# Revit family: Bernhardt_Design-Tables-Multipurpose-Intersection_stationary
name_source: partatom
category: Furniture
units: mm (PartAtom-declared; Revit-internal decimal feet)

## family parameters
Always vertical = Yes
Cut with Voids When Loaded = No
OmniClass Number = 23.40.20.00
OmniClass Title = General Furniture and Specialties
Room Calculation Point = No
Shared = No
Work Plane-Based = No

## types (90) — shared parameters
Default Elevation = 0.000"
Manufacturer = Bernhardt Design
Model = Intersection
Modesty Position = 3.720"
URL = http://www.bernhardtdesign.com

## per-type parameters (varying)
| type | Catalog | Centerleg Visibility | Modesty Length Half | Modesty Panel Visibility | Rail Length | Rail Length Half | Rail Width Half | SKU | Table Length | Table Length Half | Table Width | Table Width Half | Two Centerleg Visibility |
| Intersection - FAA - 36x36 stationary | INS-FAA | No | 13.125" | No | 35.024" | 17.512" | 17.512" | INS-FAA | 36.000" | 18.000" | 36.000" | 18.000" | No |
| Intersection - FBB - 42x42 stationary | INS-FBB | No | 16.125" | No | 41.024" | 20.512" | 20.512" | INS-FBB | 42.000" | 21.000" | 42.000" | 21.000" | No |
| Intersection - FCC - 48x48 stationary | INS-FCC | No | 19.125" | No | 47.024" | 23.512" | 23.512" | INS-FCC | 48.000" | 24.000" | 48.000" | 24.000" | No |
| Intersection - FDD - 54x54 stationary w/ modesty | INS-FDD | No | 22.125" | Yes | 53.024" | 26.512" | 26.512" | INS-FDD | 54.000" | 27.000" | 54.000" | 27.000" | No |
| Intersection - FDD - 54x54 stationary | INS-FDD | No | 22.125" | No | 53.024" | 26.512" | 26.512" | INS-FDD | 54.000" | 27.000" | 54.000" | 27.000" | No |
| Intersection - FVC - 48x24 stationary | INS-FVC | No | 19.125" | No | 47.024" | 23.512" | 11.512" | INS-FVC | 48.000" | 24.000" | 24.000" | 12.000" | No |
| Intersection - FVD - 54x24 stationary | INS-FVD | No | 22.125" | No | 53.024" | 26.512" | 11.512" | INS-FVD | 54.000" | 27.000" | 24.000" | 12.000" | No |
| Intersection - FVD - 54x24 stationary w/ modesty | INS-FVD | No | 22.125" | Yes | 53.024" | 26.512" | 11.512" | INS-FVD | 54.000" | 27.000" | 24.000" | 12.000" | No |
| Intersection - FVE - 60x24 stationary | INS-FVE | No | 25.125" | No | 59.024" | 29.512" | 11.512" | INS-FVE | 60.000" | 30.000" | 24.000" | 12.000" | No |
| Intersection - FVE - 60x24 stationary w/ modesty | INS-FVE | No | 25.125" | Yes | 59.024" | 29.512" | 11.512" | INS-FVE | 60.000" | 30.000" | 24.000" | 12.000" | No |
| Intersection - FVF - 66x24 stationary | INS-FVF | No | 28.125" | No | 65.024" | 32.512" | 11.512" | INS-FVF | 66.000" | 33.000" | 24.000" | 12.000" | No |
| Intersection - FVF - 66x24 stationary w/ modesty | INS-FVF | No | 28.125" | Yes | 65.024" | 32.512" | 11.512" | INS-FVF | 66.000" | 33.000" | 24.000" | 12.000" | No |
| Intersection - FVG - 72x24 stationary | INS-FVG | No | 31.125" | No | 71.024" | 35.512" | 11.512" | INS-FVG | 72.000" | 36.000" | 24.000" | 12.000" | No |
| Intersection - FVG - 72x24 stationary w/ modesty | INS-FVG | No | 31.125" | Yes | 71.024" | 35.512" | 11.512" | INS-FVG | 72.000" | 36.000" | 24.000" | 12.000" | No |
| Intersection - FVH - 78x24 stationary | INS-FVH | No | 34.125" | No | 77.024" | 38.512" | 11.512" | INS-FVH | 78.000" | 39.000" | 24.000" | 12.000" | No |
| Intersection - FVH - 78x24 stationary w/ modesty | INS-FVH | No | 34.125" | Yes | 77.024" | 38.512" | 11.512" | INS-FVH | 78.000" | 39.000" | 24.000" | 12.000" | No |
| Intersection - FVI - 84x24 stationary | INS-FVI | No | 37.125" | No | 83.024" | 41.512" | 11.512" | INS-FVI | 84.000" | 42.000" | 24.000" | 12.000" | No |
| Intersection - FVI - 84x24 stationary w/ modesty | INS-FVI | No | 37.125" | Yes | 83.024" | 41.512" | 11.512" | INS-FVI | 84.000" | 42.000" | 24.000" | 12.000" | No |
| Intersection - FVJ - 90x24 stationary | INS-FVJ | No | 40.125" | No | 89.024" | 44.512" | 11.512" | INS-FVJ | 90.000" | 45.000" | 24.000" | 12.000" | No |
| Intersection - FOD - 54x30 stationary | INS-FOD | No | 22.125" | No | 53.024" | 26.512" | 14.512" | INS-FOD | 54.000" | 27.000" | 30.000" | 15.000" | No |
| Intersection - FOD - 54x30 stationary w/ modesty | INS-FOD | No | 22.125" | Yes | 53.024" | 26.512" | 14.512" | INS-FOD | 54.000" | 27.000" | 30.000" | 15.000" | No |
| Intersection - FOE - 60x30 stationary | INS-FOE | No | 25.125" | No | 59.024" | 29.512" | 14.512" | INS-FOE | 60.000" | 30.000" | 30.000" | 15.000" | No |
| Intersection - FOE - 60x30 stationary w/ modesty | INS-FOE | No | 25.125" | Yes | 59.024" | 29.512" | 14.512" | INS-FOE | 60.000" | 30.000" | 30.000" | 15.000" | No |
| Intersection - FOF - 66x30 stationary | INS-FOF | No | 28.125" | No | 65.024" | 32.512" | 14.512" | INS-FOF | 66.000" | 33.000" | 30.000" | 15.000" | No |
| Intersection - FOF - 66x30 stationary w/ modesty | INS-FOF | No | 28.125" | Yes | 65.024" | 32.512" | 14.512" | INS-FOF | 66.000" | 33.000" | 30.000" | 15.000" | No |
| Intersection - FOG - 72x30 stationary | INS-FOG | No | 31.125" | No | 71.024" | 35.512" | 14.512" | INS-FOG | 72.000" | 36.000" | 30.000" | 15.000" | No |
| Intersection - FOG - 72x30 stationary w/ modesty | INS-FOG | No | 31.125" | Yes | 71.024" | 35.512" | 14.512" | INS-FOG | 72.000" | 36.000" | 30.000" | 15.000" | No |
| Intersection - FOH - 78x30 stationary | INS-FOH | No | 34.125" | No | 77.024" | 38.512" | 14.512" | INS-FOH | 78.000" | 39.000" | 30.000" | 15.000" | No |
| Intersection - FOH - 78x30 stationary w/ modesty | INS-FOH | No | 34.125" | Yes | 77.024" | 38.512" | 14.512" | INS-FOH | 78.000" | 39.000" | 30.000" | 15.000" | No |
| Intersection - FOI - 84x30 stationary | INS-FOI | No | 37.125" | No | 83.024" | 41.512" | 14.512" | INS-FOI | 84.000" | 42.000" | 30.000" | 15.000" | No |
| Intersection - FOI - 84x30 stationary w/ modesty | INS-FOI | No | 37.125" | Yes | 83.024" | 41.512" | 14.512" | INS-FOI | 84.000" | 42.000" | 30.000" | 15.000" | No |
| Intersection - FOJ - 90x30 stationary | INS-FOJ | No | 40.125" | No | 89.024" | 44.512" | 14.512" | INS-FOJ | 90.000" | 45.000" | 30.000" | 15.000" | No |
| Intersection - FAE - 60x36 stationary | INS-FAE | No | 25.125" | No | 59.024" | 29.512" | 17.512" | INS-FAE | 60.000" | 30.000" | 36.000" | 18.000" | No |
| Intersection - FAE - 60x36 stationary w/ modesty | INS-FAE | No | 25.125" | Yes | 59.024" | 29.512" | 17.512" | INS-FAE | 60.000" | 30.000" | 36.000" | 18.000" | No |
| Intersection - FAF - 66x36 stationary | INS-FAF | No | 28.125" | No | 65.024" | 32.512" | 17.512" | INS-FAF | 66.000" | 33.000" | 36.000" | 18.000" | No |
| Intersection - FAF - 66x36 stationary w/ modesty | INS-FAF | No | 28.125" | Yes | 65.024" | 32.512" | 17.512" | INS-FAF | 66.000" | 33.000" | 36.000" | 18.000" | No |
| Intersection - FAG - 72x36 stationary | INS-FAG | No | 31.125" | No | 71.024" | 35.512" | 17.512" | INS-FAG | 72.000" | 36.000" | 36.000" | 18.000" | No |
| Intersection - FAG - 72x36 stationary w/ modesty | INS-FAG | No | 31.125" | Yes | 71.024" | 35.512" | 17.512" | INS-FAG | 72.000" | 36.000" | 36.000" | 18.000" | No |
| Intersection - FAH - 78x36 stationary | INS-FAH | No | 34.125" | No | 77.024" | 38.512" | 17.512" | INS-FAH | 78.000" | 39.000" | 36.000" | 18.000" | No |
| Intersection - FAH - 78x36 stationary w/ modesty | INS-FAH | No | 34.125" | Yes | 77.024" | 38.512" | 17.512" | INS-FAH | 78.000" | 39.000" | 36.000" | 18.000" | No |
| Intersection - FAI - 84x36 stationary | INS-FAI | No | 37.125" | No | 83.024" | 41.512" | 17.512" | INS-FAI | 84.000" | 42.000" | 36.000" | 18.000" | No |
| Intersection - FAI - 84x36 stationary w/ modesty | INS-FAI | No | 37.125" | Yes | 83.024" | 41.512" | 17.512" | INS-FAI | 84.000" | 42.000" | 36.000" | 18.000" | No |
| Intersection - FAJ -90x36 stationary | INS-FAJ | No | 40.125" | No | 89.024" | 44.512" | 17.512" | INS-FAJ | 90.000" | 45.000" | 36.000" | 18.000" | No |
| Intersection - FAK - 96x36 stationary | INS-FAK | Yes | 43.125" | No | 95.024" | 47.512" | 17.512" | INS-FAK | 96.000" | 48.000" | 36.000" | 18.000" | No |
| Intersection - FAL - 102x36 stationary | INS-FAL | Yes | 46.125" | No | 101.024" | 50.512" | 17.512" | INS-FAL | 102.000" | 51.000" | 36.000" | 18.000" | No |
| Intersection - FAM - 108x36 stationary | INS-FAM | Yes | 49.125" | No | 107.024" | 53.512" | 17.512" | INS-FAM | 108.000" | 54.000" | 36.000" | 18.000" | No |
| Intersection - FBE - 60x42 stationary | INS-FBE | No | 25.125" | No | 59.024" | 29.512" | 20.512" | INS-FBE | 60.000" | 30.000" | 42.000" | 21.000" | No |
| Intersection - FBE - 60x42 stationary w/ modesty | INS-FBE | No | 25.125" | Yes | 59.024" | 29.512" | 20.512" | INS-FBE | 60.000" | 30.000" | 42.000" | 21.000" | No |
| Intersection - FBF - 66x42 stationary | INS-FBF | No | 28.125" | No | 65.024" | 32.512" | 20.512" | INS-FBF | 66.000" | 33.000" | 42.000" | 21.000" | No |
| Intersection - FBF - 66x42 stationary w/ modesty | INS-FBF | No | 28.125" | Yes | 65.024" | 32.512" | 20.512" | INS-FBF | 66.000" | 33.000" | 42.000" | 21.000" | No |
| Intersection - FBG - 72x42 stationary | INS-FBG | No | 31.125" | No | 71.024" | 35.512" | 20.512" | INS-FBG | 72.000" | 36.000" | 42.000" | 21.000" | No |
| Intersection - FBG - 72x42 stationary w/ modesty | INS-FBG | No | 31.125" | Yes | 71.024" | 35.512" | 20.512" | INS-FBG | 72.000" | 36.000" | 42.000" | 21.000" | No |
| Intersection - FBH - 78x42 stationary | INS-FBH | No | 34.125" | No | 77.024" | 38.512" | 20.512" | INS-FBH | 78.000" | 39.000" | 42.000" | 21.000" | No |
| Intersection - FBH - 78x42 stationary w/ modesty | INS-FBH | No | 34.125" | Yes | 77.024" | 38.512" | 20.512" | INS-FBH | 78.000" | 39.000" | 42.000" | 21.000" | No |
| Intersection - FBI - 84x42 stationary | INS-FBI | No | 37.125" | No | 83.024" | 41.512" | 20.512" | INS-FBI | 84.000" | 42.000" | 42.000" | 21.000" | No |
| Intersection - FBI - 84x42 stationary w/ modesty | INS-FBI | No | 37.125" | Yes | 83.024" | 41.512" | 20.512" | INS-FBI | 84.000" | 42.000" | 42.000" | 21.000" | No |
| Intersection - FBJ - 90x42 stationary | INS-FBJ | No | 40.125" | No | 89.024" | 44.512" | 20.512" | INS-FBJ | 90.000" | 45.000" | 42.000" | 21.000" | No |
| Intersection - FBK - 96x42 stationary | INS-FBK | Yes | 43.125" | No | 95.024" | 47.512" | 20.512" | INS-FBK | 96.000" | 48.000" | 42.000" | 21.000" | No |
| Intersection - FBL - 102x42 stationary | INS-FBL | Yes | 46.125" | No | 101.024" | 50.512" | 20.512" | INS-FBL | 102.000" | 51.000" | 42.000" | 21.000" | No |
| Intersection - FBM - 108x42 stationary | INS-FBM | Yes | 49.125" | No | 107.024" | 53.512" | 20.512" | INS-FBM | 108.000" | 54.000" | 42.000" | 21.000" | No |
| Intersection - FBN - 114x42 stationary | INS-FBN | No | 52.125" | No | 113.024" | 56.512" | 20.512" | INS-FBN | 114.000" | 57.000" | 42.000" | 21.000" | Yes |
| Intersection - FBO - 120x42 stationary | INS-FBO | No | 55.125" | No | 119.024" | 59.512" | 20.512" | INS-FBO | 120.000" | 60.000" | 42.000" | 21.000" | Yes |
| Intersection - FCE - 60x48 stationary | INS-FCE | No | 25.125" | No | 59.024" | 29.512" | 23.512" | INS-FCE | 60.000" | 30.000" | 48.000" | 24.000" | No |
| Intersection - FCE - 60x48 stationary w/ modesty | INS-FCE | No | 25.125" | Yes | 59.024" | 29.512" | 23.512" | INS-FCE | 60.000" | 30.000" | 48.000" | 24.000" | No |
| Intersection - FCF - 66x48 stationary | INS-FCF | No | 28.125" | No | 65.024" | 32.512" | 23.512" | INS-FCF | 66.000" | 33.000" | 48.000" | 24.000" | No |
| Intersection - FCF - 66x48 stationary w/ modesty | INS-FCF | No | 28.125" | Yes | 65.024" | 32.512" | 23.512" | INS-FCF | 66.000" | 33.000" | 48.000" | 24.000" | No |
| Intersection - FCG - 72x48 stationary | INS-FCG | No | 31.125" | No | 71.024" | 35.512" | 23.512" | INS-FCG | 72.000" | 36.000" | 48.000" | 24.000" | No |
| Intersection - FCG - 72x48 stationary w/ modesty | INS-FCG | No | 31.125" | Yes | 71.024" | 35.512" | 23.512" | INS-FCG | 72.000" | 36.000" | 48.000" | 24.000" | No |
| Intersection - FCH - 78x48 stationary | INS-FCH | No | 34.125" | No | 77.024" | 38.512" | 23.512" | INS-FCH | 78.000" | 39.000" | 48.000" | 24.000" | No |
| Intersection - FCH - 78x48 stationary w/ modesty | INS-FCH | No | 34.125" | Yes | 77.024" | 38.512" | 23.512" | INS-FCH | 78.000" | 39.000" | 48.000" | 24.000" | No |
| Intersection - FCI - 84x48 stationary | INS-FCI | No | 37.125" | No | 83.024" | 41.512" | 23.512" | INS-FCI | 84.000" | 42.000" | 48.000" | 24.000" | No |
| Intersection - FCI - 84x48 stationary w/ modesty | INS-FCI | No | 37.125" | Yes | 83.024" | 41.512" | 23.512" | INS-FCI | 84.000" | 42.000" | 48.000" | 24.000" | No |
| Intersection - FCJ - 90x48 stationary | INS-FCJ | No | 40.125" | No | 89.024" | 44.512" | 23.512" | INS-FCJ | 90.000" | 45.000" | 48.000" | 24.000" | No |
| Intersection - FCK - 96x48 stationary | INS-FCK | Yes | 43.125" | No | 95.024" | 47.512" | 23.512" | INS-FCK | 96.000" | 48.000" | 48.000" | 24.000" | No |
| Intersection - FCL - 102x48 stationary | INS-FCL | Yes | 46.125" | No | 101.024" | 50.512" | 23.512" | INS-FCL | 102.000" | 51.000" | 48.000" | 24.000" | No |
| Intersection - FCM - 108x48 stationary | INS-FCM | Yes | 49.125" | No | 107.024" | 53.512" | 23.512" | INS-FCM | 108.000" | 54.000" | 48.000" | 24.000" | No |
| Intersection - FCN - 114x48 stationary | INS-FCN | No | 52.125" | No | 113.024" | 56.512" | 23.512" | INS-FCN | 114.000" | 57.000" | 48.000" | 24.000" | Yes |
| Intersection - FCO - 120x48 stationary | INS-FCO | No | 55.125" | No | 119.024" | 59.512" | 23.512" | INS-FCO | 120.000" | 60.000" | 48.000" | 24.000" | Yes |
| Intersection - FDG - 72x54 stationary | INS-FDG | No | 31.125" | No | 71.024" | 35.512" | 26.512" | INS-FDG | 72.000" | 36.000" | 54.000" | 27.000" | No |
| Intersection - FDG - 72x54 stationary w/ modesty | INS-FDG | No | 31.125" | Yes | 71.024" | 35.512" | 26.512" | INS-FDG | 72.000" | 36.000" | 54.000" | 27.000" | No |
| Intersection - FDH - 78x54 stationary | INS-FDH | No | 34.125" | No | 77.024" | 38.512" | 26.512" | INS-FDH | 78.000" | 39.000" | 54.000" | 27.000" | No |
| Intersection - FDH - 78x54 stationary w/ modesty | INS-FDH | No | 34.125" | Yes | 77.024" | 38.512" | 26.512" | INS-FDH | 78.000" | 39.000" | 54.000" | 27.000" | No |
| Intersection - FDI - 84x54 stationary | INS-FDI | No | 37.125" | No | 83.024" | 41.512" | 26.512" | INS-FDI | 84.000" | 42.000" | 54.000" | 27.000" | No |
| Intersection - FDI - 84x54 stationary w/ modesty | INS-FDI | No | 37.125" | Yes | 83.024" | 41.512" | 26.512" | INS-FDI | 84.000" | 42.000" | 54.000" | 27.000" | No |
| Intersection - FDJ - 90x54 stationary | INS-FDJ | No | 40.125" | No | 89.024" | 44.512" | 26.512" | INS-FDJ | 90.000" | 45.000" | 54.000" | 27.000" | No |
| Intersection - FDK - 96x54 stationary | INS-FDK | Yes | 43.125" | No | 95.024" | 47.512" | 26.512" | INS-FDK | 96.000" | 48.000" | 54.000" | 27.000" | No |
| Intersection - FDL - 102x54 stationary | INS-FDL | Yes | 46.125" | No | 101.024" | 50.512" | 26.512" | INS-FDL | 102.000" | 51.000" | 54.000" | 27.000" | No |
| Intersection - FDM - 108x54 stationary | INS-FDM | Yes | 49.125" | No | 107.024" | 53.512" | 26.512" | INS-FDM | 108.000" | 54.000" | 54.000" | 27.000" | No |
| Intersection - FDN - 114x54 stationary | INS-FDN | No | 52.125" | No | 113.024" | 56.512" | 26.512" | INS-FDN | 114.000" | 57.000" | 54.000" | 27.000" | Yes |
| Intersection - FDO - 120x54 stationary | INS-FDO | No | 55.125" | No | 119.024" | 59.512" | 26.512" | INS-FDO | 120.000" | 60.000" | 54.000" | 27.000" | Yes |

## geometry (parser evidence)
native form markers: Sweep x2
no freeform markers — native parametric forms only
